# Revit family: 306_367ae2b7cdfd44e5b5a00f0199e545
name_source: partatom
category: Pipe Accessories
revit_build: Autodesk Revit 2018 (Build: 20170223_1515(x64)
units: mm (PartAtom-declared; Revit-internal decimal feet)

## family parameters
Always vertical = Yes
Cut with Voids When Loaded = No
Part Type = Valve - Breaks Into
Round Connector Dimension = Use Diameter
Shared = No
Work Plane-Based = No

## types (6) — shared parameters
CAT0 = Yes
CenSd_SW2_6 = 32 mm
D1R = 29 mm  [stored 0.0951444 ft]
Description = Pressure Reducing Valve made of gunmetal
L2D_Min = 3048 mm
Manufacturer = SYR
QmdConnectorList = 301;D;302;D
R10 = 32 mm
R6 = 19 mm
R7 = 20 mm
R8 = 23 mm
R9 = 29 mm  [stored 0.0951444 ft]
SW2 = 38 mm
magiPartTypeId = 306
magiProductFamilyId = 367ae2b7cdfd44e5b5a00f0199e545

## per-type parameters (varying)
- SYR-315-15: CenSd_SW1_6=11 mm; D=15 mm; H=123 mm; H1=14 mm  [stored 0.0459318 ft]; H2=28 mm  [stored 0.0918635 ft]; H3=22 mm; H4=62 mm; H5=8 mm  [stored 0.0262467 ft]; L10=7 mm  [stored 0.0229659 ft]; L11=12 mm  [stored 0.0393701 ft]; L11__ve=-12 mm; L2=66 mm; L2D=132 mm; L4=38 mm; L6=66 mm; L8=33 mm  [stored 0.108268 ft]; L9=11 mm; L9__ve=-11 mm  [stored -0.0360892 ft]; NUT=No; R11=5 mm  [stored 0.0164042 ft]; R2=9 mm  [stored 0.0295276 ft]; R3=10 mm  [stored 0.0328084 ft]; R4=11 mm; R5=27 mm  [stored 0.0885827 ft]; ROU=Yes; SW1=13 mm  [stored 0.0426509 ft]; W1=35 mm  [stored 0.114829 ft]; W2D=15 mm  [stored 0.0492126 ft]; magiProductId=6f415e7e703441e68d1f01d706a28d
- SYR-315-50: CenSd_SW1_6=30 mm  [stored 0.0984252 ft]; D=50 mm; H=180 mm; H1=36 mm; H2=72 mm; H3=29 mm  [stored 0.0951444 ft]; H4=83 mm; H5=18 mm; L10=13 mm  [stored 0.0426509 ft]; L11=22 mm; L11__ve=-22 mm; L2=128 mm; L2D=255 mm; L4=70 mm; L6=123 mm; L8=61 mm; L9=22 mm; L9__ve=-22 mm; NUT=Yes; R11=15 mm  [stored 0.0492126 ft]; R2=27 mm  [stored 0.0885827 ft]; R3=27 mm  [stored 0.0885827 ft]; R4=28 mm  [stored 0.0918635 ft]; R5=36 mm; ROU=No; SW1=35 mm  [stored 0.114829 ft]; W1=44 mm; W2D=50 mm; magiProductId=39130a2841cf4045b1c4e5bd0c0383
- SYR-315-40: CenSd_SW1_6=26 mm; D=40 mm; H=176 mm; H1=31 mm; H2=62 mm; H3=29 mm  [stored 0.0951444 ft]; H4=84 mm; H5=15 mm  [stored 0.0492126 ft]; L10=12 mm  [stored 0.0393701 ft]; L11=20 mm; L11__ve=-20 mm; L2=110 mm; L2D=220 mm; L4=65 mm; L6=114 mm; L8=57 mm; L9=16 mm; L9__ve=-16 mm; NUT=Yes; R11=12 mm  [stored 0.0393701 ft]; R2=22 mm; R3=22 mm; R4=23 mm; R5=36 mm; ROU=No; SW1=30 mm  [stored 0.0984252 ft]; W1=44 mm; W2D=40 mm; magiProductId=2c0b15c4ad4f444ea2b7d157964fe1
- SYR-315-32: CenSd_SW1_6=22 mm; D=32 mm; H=176 mm; H1=26 mm; H2=52 mm; H3=30 mm  [stored 0.0984252 ft]; H4=87 mm; H5=13 mm  [stored 0.0426509 ft]; L10=8 mm  [stored 0.0262467 ft]; L11=14 mm  [stored 0.0459318 ft]; L11__ve=-14 mm  [stored -0.0459318 ft]; L2=95 mm; L2D=190 mm; L4=44 mm; L6=76 mm; L8=38 mm; L9=22 mm; L9__ve=-22 mm; NUT=Yes; R11=10 mm  [stored 0.0328084 ft]; R2=18 mm; R3=18 mm; R4=19 mm; R5=36 mm; ROU=No; SW1=25 mm  [stored 0.082021 ft]; W1=44 mm; W2D=32 mm; magiProductId=272084d937e54867bee0e6795c34e3
- SYR-315-25: CenSd_SW1_6=17 mm; D=25 mm; H=121 mm; H1=21 mm; H2=42 mm; H3=20 mm; H4=57 mm; H5=11 mm; L10=8 mm  [stored 0.0262467 ft]; L11=14 mm  [stored 0.0459318 ft]; L11__ve=-14 mm  [stored -0.0459318 ft]; L2=81 mm; L2D=161 mm; L4=44 mm; L6=76 mm; L8=38 mm; L9=14 mm  [stored 0.0459318 ft]; L9__ve=-14 mm  [stored -0.0459318 ft]; NUT=No; R11=8 mm  [stored 0.0262467 ft]; R2=14 mm  [stored 0.0459318 ft]; R3=15 mm  [stored 0.0492126 ft]; R4=16 mm; R5=27 mm  [stored 0.0885827 ft]; ROU=Yes; SW1=20 mm; W1=35 mm  [stored 0.114829 ft]; W2D=25 mm  [stored 0.082021 ft]; magiProductId=e0f22559d902489399b1557e3db8ca
- SYR-315-20: CenSd_SW1_6=15 mm  [stored 0.0492126 ft]; D=20 mm; H=123 mm; H1=18 mm; H2=36 mm; H3=21 mm; H4=60 mm; H5=9 mm  [stored 0.0295276 ft]; L10=7 mm  [stored 0.0229659 ft]; L11=12 mm  [stored 0.0393701 ft]; L11__ve=-12 mm; L2=72 mm; L2D=143 mm; L4=38 mm; L6=66 mm; L8=33 mm  [stored 0.108268 ft]; L9=13 mm  [stored 0.0426509 ft]; L9__ve=-13 mm  [stored -0.0426509 ft]; NUT=No; R11=6 mm  [stored 0.019685 ft]; R2=12 mm  [stored 0.0393701 ft]; R3=12 mm  [stored 0.0393701 ft]; R4=13 mm  [stored 0.0426509 ft]; R5=27 mm  [stored 0.0885827 ft]; ROU=Yes; SW1=17 mm; W1=35 mm  [stored 0.114829 ft]; W2D=20 mm; magiProductId=55d250b5ea194f0087609e8d1728e6

note: column(s) folded — value = type name in every type: MC Product Code

note: [stored X ft] marks values corroborated as IEEE doubles in the binary element streams (Revit-internal decimal feet)

## geometry (parser evidence)
native form markers: Sweep x2
no freeform markers — native parametric forms only
